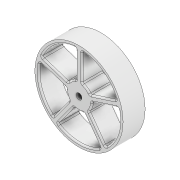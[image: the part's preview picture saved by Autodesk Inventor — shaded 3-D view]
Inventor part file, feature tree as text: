
AUTODESK INVENTOR PART (.ipt)
format: ipt  version: 2020 (Build 240168000, 168)  size: 297,984 bytes
history: native  units: mm
features: other x1, extrude x1, fillet x1, sketch x1
ambient origin geometry x8: Origin, YZ Plane, XZ Plane, XY Plane, X Axis, Y Axis, Z Axis, Center Point
bodies: Body1 (feature_tree)
feature tree (4):
  other  "솔리드1"
  extrude  "돌출1"  Depth=50.0mm TaperAngle=360.0deg
  fillet  "모깎기1"  Radius=120.0mm
  sketch  "스케치1"
